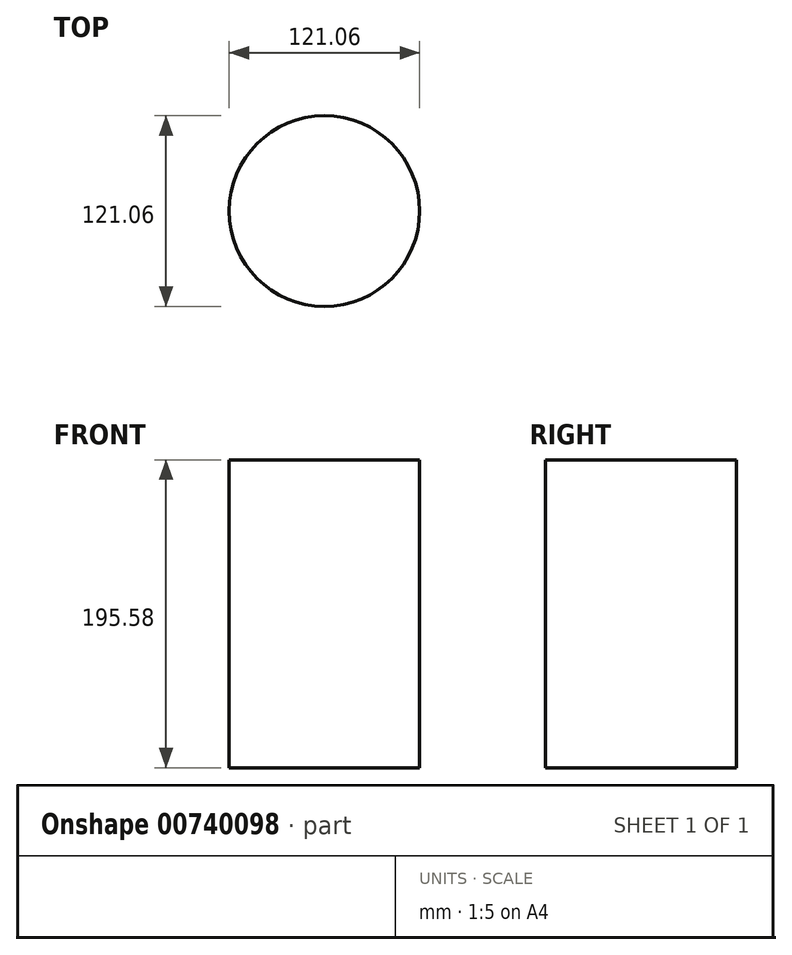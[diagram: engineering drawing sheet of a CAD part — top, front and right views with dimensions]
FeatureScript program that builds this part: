
annotation { "Feature Type Name" : "Feature", "Feature Type Description" : "" }
export const myFeature = defineFeature(function(context is Context, id is Id, definition is map)
    precondition{}
    {
        {
            var Q0;
            Q0=qCreatedBy(makeId("Top.planeOp"),FACE);
            var sketch = newSketch(context, id + "F0", { "sketchPlane" : qUnion([Q0])});
            skCircle(sketch, "E0", {"center": v(0, 0) * mm, "radius": 60.53 * mm});
            skSolve(sketch);
        }
        {
            var Q0;
            Q0 = qSketchRegion(id + "F0", true);
            extrude(context, id + "F1", {"entities" : qUnion([Q0]), "depth" : 195.58 * mm, "offsetDistance" : 25.4 * mm});
        }
    });
